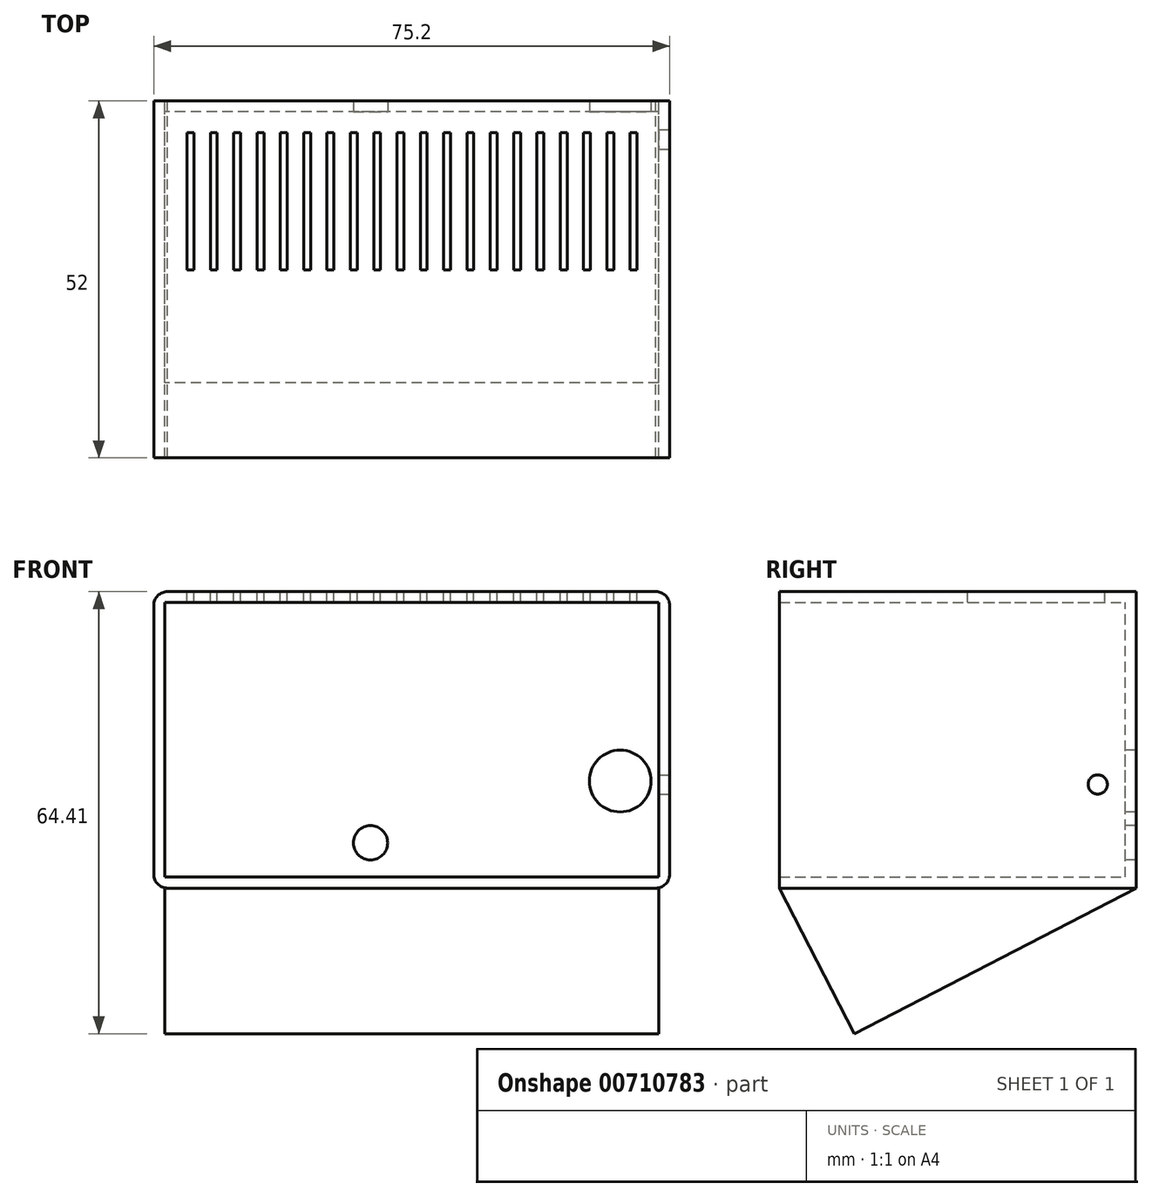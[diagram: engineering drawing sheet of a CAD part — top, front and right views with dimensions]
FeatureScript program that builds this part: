
annotation { "Feature Type Name" : "Feature", "Feature Type Description" : "" }
export const myFeature = defineFeature(function(context is Context, id is Id, definition is map)
    precondition{}
    {
        {
            var Q0;
            Q0=qCreatedBy(makeId("Front.planeOp"),FACE);
            var sketch = newSketch(context, id + "F0", { "sketchPlane" : qUnion([Q0])});
            skLineSegment(sketch, "E0.bottom", {"start": v(36, -20) * mm, "end": v(-36, -20) * mm});
            skLineSegment(sketch, "E0.top", {"start": v(36, 20) * mm, "end": v(-36, 20) * mm});
            skLineSegment(sketch, "E0.left", {"start": v(36, -20) * mm, "end": v(36, 20) * mm});
            skLineSegment(sketch, "E0.right", {"start": v(-36, -20) * mm, "end": v(-36, 20) * mm});
            skPoint(sketch, "E0.middle", {"position": v(0, 0) * mm});
            skLineSegment(sketch, "E1.0", {"start": v(-37.6, -21.6) * mm, "end": v(-37.6, 21.6) * mm});
            skLineSegment(sketch, "E1.1", {"start": v(37.6, -21.6) * mm, "end": v(-37.6, -21.6) * mm});
            skLineSegment(sketch, "E1.2", {"start": v(37.6, -21.6) * mm, "end": v(37.6, 21.6) * mm});
            skLineSegment(sketch, "E1.3", {"start": v(37.6, 21.6) * mm, "end": v(-37.6, 21.6) * mm});
            skPoint(sketch, "E2", {"position": v(30.4, -6) * mm});
            skPoint(sketch, "E3", {"position": v(-6, -15) * mm});
            skSolve(sketch);
        }
        {
            var Q0;
            Q0=makeQuery(id+"F0.imprint","IMPRINT",FACE,{"disambiguationData":[TD([[makeQuery(id+"F0.imprint","IMPRINT",EDGE,{"derivedFrom":sQuery(id+"F0.wireOp",EDGE,"E0.bottom")}),1.0]])]});
            extrude(context, id + "F1", {"entities" : qUnion([Q0]), "depth" : 52 * mm, "offsetDistance" : 25 * mm});
        }
        {
            var Q0;
            Q0=makeQuery(id+"F1.opExtrude","SWEPT_EDGE",EDGE,{"disambiguationData":[OSD([sQuery(id+"F0.wireOp",EDGE,"E1.2"),sQuery(id+"F0.wireOp",EDGE,"E1.3")])]});
            var Q1;
            Q1=makeQuery(id+"F1.opExtrude","SWEPT_EDGE",EDGE,{"disambiguationData":[OSD([sQuery(id+"F0.wireOp",EDGE,"E1.0"),sQuery(id+"F0.wireOp",EDGE,"E1.3")])]});
            var Q2;
            Q2=makeQuery(id+"F1.opExtrude","SWEPT_EDGE",EDGE,{"disambiguationData":[OSD([sQuery(id+"F0.wireOp",EDGE,"E1.0"),sQuery(id+"F0.wireOp",EDGE,"E1.1")])]});
            var Q3;
            Q3=makeQuery(id+"F1.opExtrude","SWEPT_EDGE",EDGE,{"disambiguationData":[OSD([sQuery(id+"F0.wireOp",EDGE,"E1.1"),sQuery(id+"F0.wireOp",EDGE,"E1.2")])]});
            fillet(context, id + "F2", {"entities" : qUnion([Q0, Q1, Q2, Q3]), "radius" : 2 * mm, "tangentPropagation" : true, "allowEdgeOverflow" : false});
        }
        {
            var Q0;
            Q0=makeQuery(id+"F0.imprint","IMPRINT",FACE,{"disambiguationData":[TD([[makeQuery(id+"F0.imprint","IMPRINT",EDGE,{"derivedFrom":sQuery(id+"F0.wireOp",EDGE,"E0.bottom")}),-1.0]])]});
            extrude(context, id + "F3", {"entities" : qUnion([Q0]), "operationType" : NewBodyOperationType.ADD, "depth" : 1.6 * mm, "offsetDistance" : 25 * mm});
        }
        {
            var Q0;
            Q0=qCreatedBy(makeId("Right.planeOp"),FACE);
            var sketch = newSketch(context, id + "F4", { "sketchPlane" : qUnion([Q0])});
            skPoint(sketch, "E4.0", {"position": v(-52, -21.6) * mm});
            skLineSegment(sketch, "E5", {"start": v(-52, -21.6) * mm, "end": v(-41.04, -42.8) * mm});
            skLineSegment(sketch, "E6", {"start": v(-41.04, -42.8) * mm, "end": v(0, -21.6) * mm});
            skLineSegment(sketch, "E7", {"start": v(-52, -21.6) * mm, "end": v(0, -21.6) * mm});
            skSolve(sketch);
        }
        {
            var Q0;
            Q0=makeQuery(id+"F4.imprint","IMPRINT",FACE,{"disambiguationData":[TD([[makeQuery(id+"F4.imprint","IMPRINT",EDGE,{"derivedFrom":sQuery(id+"F4.wireOp",EDGE,"E5")}),1.0]])]});
            extrude(context, id + "F5", {"entities" : qUnion([Q0]), "operationType" : NewBodyOperationType.ADD, "depth" : 72 * mm, "offsetDistance" : 25 * mm, "symmetric" : true});
        }
        {
            var Q0;
            Q0=sQuery(id+"F0.wireOp",VERTEX,"E2");
            var Q1;
            Q1=makeQuery(id+"F1.opExtrude","SWEPT_BODY",BODY,{"disambiguationData":[OSD([sQuery(id+"F0.wireOp",EDGE,"E0.bottom"),sQuery(id+"F0.wireOp",EDGE,"E0.top"),sQuery(id+"F0.wireOp",EDGE,"E0.left"),sQuery(id+"F0.wireOp",EDGE,"E0.right"),sQuery(id+"F0.wireOp",EDGE,"E1.0"),sQuery(id+"F0.wireOp",EDGE,"E1.1"),sQuery(id+"F0.wireOp",EDGE,"E1.2"),sQuery(id+"F0.wireOp",EDGE,"E1.3")])]});
            hole(context, id + "F6", {"style" : HoleStyle.SIMPLE, "endStyle" : HoleEndStyle.THROUGH, "oppositeDirection" : true, "holeDiameter" : 9 * mm, "majorDiameter" : 5 * mm, "isTappedThrough" : true, "tappedDepth" : 12 * mm, "tapClearance" : 3, "locations" : qUnion([Q0]), "scope" : qUnion([Q1])});
        }
        {
            var Q0;
            Q0=makeQuery(id+"F1.opExtrude","SWEPT_FACE",FACE,{"disambiguationData":[OSD([sQuery(id+"F0.wireOp",EDGE,"E0.left")])]});
            var sketch = newSketch(context, id + "F7", { "sketchPlane" : qUnion([Q0])});
            skPoint(sketch, "E8", {"position": v(5.6, -6.5) * mm});
            skSolve(sketch);
        }
        {
            var Q0;
            Q0=sQuery(id+"F7.wireOp",VERTEX,"E8");
            var Q1;
            Q1=makeQuery(id+"F1.opExtrude","SWEPT_BODY",BODY,{"disambiguationData":[OSD([sQuery(id+"F0.wireOp",EDGE,"E0.bottom"),sQuery(id+"F0.wireOp",EDGE,"E0.top"),sQuery(id+"F0.wireOp",EDGE,"E0.left"),sQuery(id+"F0.wireOp",EDGE,"E0.right"),sQuery(id+"F0.wireOp",EDGE,"E1.0"),sQuery(id+"F0.wireOp",EDGE,"E1.1"),sQuery(id+"F0.wireOp",EDGE,"E1.2"),sQuery(id+"F0.wireOp",EDGE,"E1.3")])]});
            hole(context, id + "F8", {"style" : HoleStyle.SIMPLE, "endStyle" : HoleEndStyle.THROUGH, "holeDiameter" : 2.8 * mm, "majorDiameter" : 5 * mm, "isTappedThrough" : true, "tappedDepth" : 12 * mm, "tapClearance" : 3, "locations" : qUnion([Q0]), "scope" : qUnion([Q1])});
        }
        {
            var Q0;
            Q0=sQuery(id+"F0.wireOp",VERTEX,"E3");
            var Q1;
            Q1=makeQuery(id+"F1.opExtrude","SWEPT_BODY",BODY,{"disambiguationData":[OSD([sQuery(id+"F0.wireOp",EDGE,"E0.bottom"),sQuery(id+"F0.wireOp",EDGE,"E0.top"),sQuery(id+"F0.wireOp",EDGE,"E0.left"),sQuery(id+"F0.wireOp",EDGE,"E0.right"),sQuery(id+"F0.wireOp",EDGE,"E1.0"),sQuery(id+"F0.wireOp",EDGE,"E1.1"),sQuery(id+"F0.wireOp",EDGE,"E1.2"),sQuery(id+"F0.wireOp",EDGE,"E1.3")])]});
            hole(context, id + "F9", {"style" : HoleStyle.SIMPLE, "endStyle" : HoleEndStyle.THROUGH, "oppositeDirection" : true, "holeDiameter" : 5 * mm, "majorDiameter" : 5 * mm, "isTappedThrough" : true, "tappedDepth" : 12 * mm, "tapClearance" : 3, "locations" : qUnion([Q0]), "scope" : qUnion([Q1])});
        }
        {
            var Q0;
            Q0=makeQuery(id+"F1.opExtrude","SWEPT_FACE",FACE,{"disambiguationData":[OSD([sQuery(id+"F0.wireOp",EDGE,"E1.3")])]});
            var sketch = newSketch(context, id + "F10", { "sketchPlane" : qUnion([Q0])});
            skLineSegment(sketch, "E9.bottom", {"start": v(-32.74, -4.6) * mm, "end": v(-31.74, -4.6) * mm});
            skLineSegment(sketch, "E9.top", {"start": v(-32.74, -24.6) * mm, "end": v(-31.74, -24.6) * mm});
            skLineSegment(sketch, "E9.left", {"start": v(-32.74, -4.6) * mm, "end": v(-32.74, -24.6) * mm});
            skLineSegment(sketch, "E9.right", {"start": v(-31.74, -4.6) * mm, "end": v(-31.74, -24.6) * mm});
            skLineSegment(sketch, "E10.1.0.0", {"start": v(-29.34, -4.6) * mm, "end": v(-28.34, -4.6) * mm});
            skLineSegment(sketch, "E10.1.0.1", {"start": v(-29.34, -4.6) * mm, "end": v(-29.34, -24.6) * mm});
            skLineSegment(sketch, "E10.1.0.2", {"start": v(-28.34, -4.6) * mm, "end": v(-28.34, -24.6) * mm});
            skLineSegment(sketch, "E10.1.0.3", {"start": v(-29.34, -24.6) * mm, "end": v(-28.34, -24.6) * mm});
            skLineSegment(sketch, "E10.2.0.0", {"start": v(-25.94, -4.6) * mm, "end": v(-24.94, -4.6) * mm});
            skLineSegment(sketch, "E10.2.0.1", {"start": v(-25.94, -4.6) * mm, "end": v(-25.94, -24.6) * mm});
            skLineSegment(sketch, "E10.2.0.2", {"start": v(-24.94, -4.6) * mm, "end": v(-24.94, -24.6) * mm});
            skLineSegment(sketch, "E10.2.0.3", {"start": v(-25.94, -24.6) * mm, "end": v(-24.94, -24.6) * mm});
            skLineSegment(sketch, "E10.3.0.0", {"start": v(-22.54, -4.6) * mm, "end": v(-21.54, -4.6) * mm});
            skLineSegment(sketch, "E10.3.0.1", {"start": v(-22.54, -4.6) * mm, "end": v(-22.54, -24.6) * mm});
            skLineSegment(sketch, "E10.3.0.2", {"start": v(-21.54, -4.6) * mm, "end": v(-21.54, -24.6) * mm});
            skLineSegment(sketch, "E10.3.0.3", {"start": v(-22.54, -24.6) * mm, "end": v(-21.54, -24.6) * mm});
            skLineSegment(sketch, "E10.4.0.0", {"start": v(-19.14, -4.6) * mm, "end": v(-18.14, -4.6) * mm});
            skLineSegment(sketch, "E10.4.0.1", {"start": v(-19.14, -4.6) * mm, "end": v(-19.14, -24.6) * mm});
            skLineSegment(sketch, "E10.4.0.2", {"start": v(-18.14, -4.6) * mm, "end": v(-18.14, -24.6) * mm});
            skLineSegment(sketch, "E10.4.0.3", {"start": v(-19.14, -24.6) * mm, "end": v(-18.14, -24.6) * mm});
            skLineSegment(sketch, "E10.5.0.0", {"start": v(-15.74, -4.6) * mm, "end": v(-14.74, -4.6) * mm});
            skLineSegment(sketch, "E10.5.0.1", {"start": v(-15.74, -4.6) * mm, "end": v(-15.74, -24.6) * mm});
            skLineSegment(sketch, "E10.5.0.2", {"start": v(-14.74, -4.6) * mm, "end": v(-14.74, -24.6) * mm});
            skLineSegment(sketch, "E10.5.0.3", {"start": v(-15.74, -24.6) * mm, "end": v(-14.74, -24.6) * mm});
            skLineSegment(sketch, "E10.6.0.0", {"start": v(-12.34, -4.6) * mm, "end": v(-11.34, -4.6) * mm});
            skLineSegment(sketch, "E10.6.0.1", {"start": v(-12.34, -4.6) * mm, "end": v(-12.34, -24.6) * mm});
            skLineSegment(sketch, "E10.6.0.2", {"start": v(-11.34, -4.6) * mm, "end": v(-11.34, -24.6) * mm});
            skLineSegment(sketch, "E10.6.0.3", {"start": v(-12.34, -24.6) * mm, "end": v(-11.34, -24.6) * mm});
            skLineSegment(sketch, "E10.7.0.0", {"start": v(-8.94, -4.6) * mm, "end": v(-7.94, -4.6) * mm});
            skLineSegment(sketch, "E10.7.0.1", {"start": v(-8.94, -4.6) * mm, "end": v(-8.94, -24.6) * mm});
            skLineSegment(sketch, "E10.7.0.2", {"start": v(-7.94, -4.6) * mm, "end": v(-7.94, -24.6) * mm});
            skLineSegment(sketch, "E10.7.0.3", {"start": v(-8.94, -24.6) * mm, "end": v(-7.94, -24.6) * mm});
            skLineSegment(sketch, "E10.8.0.0", {"start": v(-5.54, -4.6) * mm, "end": v(-4.54, -4.6) * mm});
            skLineSegment(sketch, "E10.8.0.1", {"start": v(-5.54, -4.6) * mm, "end": v(-5.54, -24.6) * mm});
            skLineSegment(sketch, "E10.8.0.2", {"start": v(-4.54, -4.6) * mm, "end": v(-4.54, -24.6) * mm});
            skLineSegment(sketch, "E10.8.0.3", {"start": v(-5.54, -24.6) * mm, "end": v(-4.54, -24.6) * mm});
            skLineSegment(sketch, "E10.9.0.0", {"start": v(-2.14, -4.6) * mm, "end": v(-1.14, -4.6) * mm});
            skLineSegment(sketch, "E10.9.0.1", {"start": v(-2.14, -4.6) * mm, "end": v(-2.14, -24.6) * mm});
            skLineSegment(sketch, "E10.9.0.2", {"start": v(-1.14, -4.6) * mm, "end": v(-1.14, -24.6) * mm});
            skLineSegment(sketch, "E10.9.0.3", {"start": v(-2.14, -24.6) * mm, "end": v(-1.14, -24.6) * mm});
            skLineSegment(sketch, "E10.10.0.0", {"start": v(1.26, -4.6) * mm, "end": v(2.26, -4.6) * mm});
            skLineSegment(sketch, "E10.10.0.1", {"start": v(1.26, -4.6) * mm, "end": v(1.26, -24.6) * mm});
            skLineSegment(sketch, "E10.10.0.2", {"start": v(2.26, -4.6) * mm, "end": v(2.26, -24.6) * mm});
            skLineSegment(sketch, "E10.10.0.3", {"start": v(1.26, -24.6) * mm, "end": v(2.26, -24.6) * mm});
            skLineSegment(sketch, "E10.11.0.0", {"start": v(4.66, -4.6) * mm, "end": v(5.66, -4.6) * mm});
            skLineSegment(sketch, "E10.11.0.1", {"start": v(4.66, -4.6) * mm, "end": v(4.66, -24.6) * mm});
            skLineSegment(sketch, "E10.11.0.2", {"start": v(5.66, -4.6) * mm, "end": v(5.66, -24.6) * mm});
            skLineSegment(sketch, "E10.11.0.3", {"start": v(4.66, -24.6) * mm, "end": v(5.66, -24.6) * mm});
            skLineSegment(sketch, "E10.12.0.0", {"start": v(8.06, -4.6) * mm, "end": v(9.06, -4.6) * mm});
            skLineSegment(sketch, "E10.12.0.1", {"start": v(8.06, -4.6) * mm, "end": v(8.06, -24.6) * mm});
            skLineSegment(sketch, "E10.12.0.2", {"start": v(9.06, -4.6) * mm, "end": v(9.06, -24.6) * mm});
            skLineSegment(sketch, "E10.12.0.3", {"start": v(8.06, -24.6) * mm, "end": v(9.06, -24.6) * mm});
            skLineSegment(sketch, "E10.13.0.0", {"start": v(11.46, -4.6) * mm, "end": v(12.46, -4.6) * mm});
            skLineSegment(sketch, "E10.13.0.1", {"start": v(11.46, -4.6) * mm, "end": v(11.46, -24.6) * mm});
            skLineSegment(sketch, "E10.13.0.2", {"start": v(12.46, -4.6) * mm, "end": v(12.46, -24.6) * mm});
            skLineSegment(sketch, "E10.13.0.3", {"start": v(11.46, -24.6) * mm, "end": v(12.46, -24.6) * mm});
            skLineSegment(sketch, "E10.14.0.0", {"start": v(14.86, -4.6) * mm, "end": v(15.86, -4.6) * mm});
            skLineSegment(sketch, "E10.14.0.1", {"start": v(14.86, -4.6) * mm, "end": v(14.86, -24.6) * mm});
            skLineSegment(sketch, "E10.14.0.2", {"start": v(15.86, -4.6) * mm, "end": v(15.86, -24.6) * mm});
            skLineSegment(sketch, "E10.14.0.3", {"start": v(14.86, -24.6) * mm, "end": v(15.86, -24.6) * mm});
            skLineSegment(sketch, "E10.15.0.0", {"start": v(18.26, -4.6) * mm, "end": v(19.26, -4.6) * mm});
            skLineSegment(sketch, "E10.15.0.1", {"start": v(18.26, -4.6) * mm, "end": v(18.26, -24.6) * mm});
            skLineSegment(sketch, "E10.15.0.2", {"start": v(19.26, -4.6) * mm, "end": v(19.26, -24.6) * mm});
            skLineSegment(sketch, "E10.15.0.3", {"start": v(18.26, -24.6) * mm, "end": v(19.26, -24.6) * mm});
            skLineSegment(sketch, "E10.16.0.0", {"start": v(21.66, -4.6) * mm, "end": v(22.66, -4.6) * mm});
            skLineSegment(sketch, "E10.16.0.1", {"start": v(21.66, -4.6) * mm, "end": v(21.66, -24.6) * mm});
            skLineSegment(sketch, "E10.16.0.2", {"start": v(22.66, -4.6) * mm, "end": v(22.66, -24.6) * mm});
            skLineSegment(sketch, "E10.16.0.3", {"start": v(21.66, -24.6) * mm, "end": v(22.66, -24.6) * mm});
            skLineSegment(sketch, "E10.17.0.0", {"start": v(25.06, -4.6) * mm, "end": v(26.06, -4.6) * mm});
            skLineSegment(sketch, "E10.17.0.1", {"start": v(25.06, -4.6) * mm, "end": v(25.06, -24.6) * mm});
            skLineSegment(sketch, "E10.17.0.2", {"start": v(26.06, -4.6) * mm, "end": v(26.06, -24.6) * mm});
            skLineSegment(sketch, "E10.17.0.3", {"start": v(25.06, -24.6) * mm, "end": v(26.06, -24.6) * mm});
            skLineSegment(sketch, "E10.18.0.0", {"start": v(28.46, -4.6) * mm, "end": v(29.46, -4.6) * mm});
            skLineSegment(sketch, "E10.18.0.1", {"start": v(28.46, -4.6) * mm, "end": v(28.46, -24.6) * mm});
            skLineSegment(sketch, "E10.18.0.2", {"start": v(29.46, -4.6) * mm, "end": v(29.46, -24.6) * mm});
            skLineSegment(sketch, "E10.18.0.3", {"start": v(28.46, -24.6) * mm, "end": v(29.46, -24.6) * mm});
            skLineSegment(sketch, "E10.19.0.0", {"start": v(31.86, -4.6) * mm, "end": v(32.86, -4.6) * mm});
            skLineSegment(sketch, "E10.19.0.1", {"start": v(31.86, -4.6) * mm, "end": v(31.86, -24.6) * mm});
            skLineSegment(sketch, "E10.19.0.2", {"start": v(32.86, -4.6) * mm, "end": v(32.86, -24.6) * mm});
            skLineSegment(sketch, "E10.19.0.3", {"start": v(31.86, -24.6) * mm, "end": v(32.86, -24.6) * mm});
            skLineSegment(sketch, "E10.direction1", {"start": v(-32.74, -4.6) * mm, "end": v(-29.34, -4.6) * mm, "construction": true});
            skSolve(sketch);
        }
        {
            var Q0;
            Q0=makeQuery(id+"F10.imprint","IMPRINT",FACE,{"disambiguationData":[TD([[makeQuery(id+"F10.imprint","IMPRINT",EDGE,{"derivedFrom":sQuery(id+"F10.wireOp",EDGE,"E9.bottom")}),-1.0]])]});
            var Q1;
            Q1=makeQuery(id+"F10.imprint","IMPRINT",FACE,{"disambiguationData":[TD([[makeQuery(id+"F10.imprint","IMPRINT",EDGE,{"derivedFrom":sQuery(id+"F10.wireOp",EDGE,"E10.1.0.0")}),-1.0]])]});
            var Q2;
            Q2=makeQuery(id+"F10.imprint","IMPRINT",FACE,{"disambiguationData":[TD([[makeQuery(id+"F10.imprint","IMPRINT",EDGE,{"derivedFrom":sQuery(id+"F10.wireOp",EDGE,"E10.2.0.0")}),-1.0]])]});
            var Q3;
            Q3=makeQuery(id+"F10.imprint","IMPRINT",FACE,{"disambiguationData":[TD([[makeQuery(id+"F10.imprint","IMPRINT",EDGE,{"derivedFrom":sQuery(id+"F10.wireOp",EDGE,"E10.3.0.0")}),-1.0]])]});
            var Q4;
            Q4=makeQuery(id+"F10.imprint","IMPRINT",FACE,{"disambiguationData":[TD([[makeQuery(id+"F10.imprint","IMPRINT",EDGE,{"derivedFrom":sQuery(id+"F10.wireOp",EDGE,"E10.4.0.0")}),-1.0]])]});
            var Q5;
            Q5=makeQuery(id+"F10.imprint","IMPRINT",FACE,{"disambiguationData":[TD([[makeQuery(id+"F10.imprint","IMPRINT",EDGE,{"derivedFrom":sQuery(id+"F10.wireOp",EDGE,"E10.5.0.0")}),-1.0]])]});
            var Q6;
            Q6=makeQuery(id+"F10.imprint","IMPRINT",FACE,{"disambiguationData":[TD([[makeQuery(id+"F10.imprint","IMPRINT",EDGE,{"derivedFrom":sQuery(id+"F10.wireOp",EDGE,"E10.6.0.0")}),-1.0]])]});
            var Q7;
            Q7=makeQuery(id+"F10.imprint","IMPRINT",FACE,{"disambiguationData":[TD([[makeQuery(id+"F10.imprint","IMPRINT",EDGE,{"derivedFrom":sQuery(id+"F10.wireOp",EDGE,"E10.7.0.0")}),-1.0]])]});
            var Q8;
            Q8=makeQuery(id+"F10.imprint","IMPRINT",FACE,{"disambiguationData":[TD([[makeQuery(id+"F10.imprint","IMPRINT",EDGE,{"derivedFrom":sQuery(id+"F10.wireOp",EDGE,"E10.8.0.0")}),-1.0]])]});
            var Q9;
            Q9=makeQuery(id+"F10.imprint","IMPRINT",FACE,{"disambiguationData":[TD([[makeQuery(id+"F10.imprint","IMPRINT",EDGE,{"derivedFrom":sQuery(id+"F10.wireOp",EDGE,"E10.10.0.0")}),-1.0]])]});
            var Q10;
            Q10=makeQuery(id+"F10.imprint","IMPRINT",FACE,{"disambiguationData":[TD([[makeQuery(id+"F10.imprint","IMPRINT",EDGE,{"derivedFrom":sQuery(id+"F10.wireOp",EDGE,"E10.11.0.0")}),-1.0]])]});
            var Q11;
            Q11=makeQuery(id+"F10.imprint","IMPRINT",FACE,{"disambiguationData":[TD([[makeQuery(id+"F10.imprint","IMPRINT",EDGE,{"derivedFrom":sQuery(id+"F10.wireOp",EDGE,"E10.9.0.0")}),-1.0]])]});
            var Q12;
            Q12=makeQuery(id+"F10.imprint","IMPRINT",FACE,{"disambiguationData":[TD([[makeQuery(id+"F10.imprint","IMPRINT",EDGE,{"derivedFrom":sQuery(id+"F10.wireOp",EDGE,"E10.12.0.0")}),-1.0]])]});
            var Q13;
            Q13=makeQuery(id+"F10.imprint","IMPRINT",FACE,{"disambiguationData":[TD([[makeQuery(id+"F10.imprint","IMPRINT",EDGE,{"derivedFrom":sQuery(id+"F10.wireOp",EDGE,"E10.13.0.0")}),-1.0]])]});
            var Q14;
            Q14=makeQuery(id+"F10.imprint","IMPRINT",FACE,{"disambiguationData":[TD([[makeQuery(id+"F10.imprint","IMPRINT",EDGE,{"derivedFrom":sQuery(id+"F10.wireOp",EDGE,"E10.14.0.0")}),-1.0]])]});
            var Q15;
            Q15=makeQuery(id+"F10.imprint","IMPRINT",FACE,{"disambiguationData":[TD([[makeQuery(id+"F10.imprint","IMPRINT",EDGE,{"derivedFrom":sQuery(id+"F10.wireOp",EDGE,"E10.15.0.0")}),-1.0]])]});
            var Q16;
            Q16=makeQuery(id+"F10.imprint","IMPRINT",FACE,{"disambiguationData":[TD([[makeQuery(id+"F10.imprint","IMPRINT",EDGE,{"derivedFrom":sQuery(id+"F10.wireOp",EDGE,"E10.16.0.0")}),-1.0]])]});
            var Q17;
            Q17=makeQuery(id+"F10.imprint","IMPRINT",FACE,{"disambiguationData":[TD([[makeQuery(id+"F10.imprint","IMPRINT",EDGE,{"derivedFrom":sQuery(id+"F10.wireOp",EDGE,"E10.17.0.0")}),-1.0]])]});
            var Q18;
            Q18=makeQuery(id+"F10.imprint","IMPRINT",FACE,{"disambiguationData":[TD([[makeQuery(id+"F10.imprint","IMPRINT",EDGE,{"derivedFrom":sQuery(id+"F10.wireOp",EDGE,"E10.18.0.0")}),-1.0]])]});
            var Q19;
            Q19=makeQuery(id+"F10.imprint","IMPRINT",FACE,{"disambiguationData":[TD([[makeQuery(id+"F10.imprint","IMPRINT",EDGE,{"derivedFrom":sQuery(id+"F10.wireOp",EDGE,"E10.19.0.0")}),-1.0]])]});
            extrude(context, id + "F11", {"entities" : qUnion([Q0, Q1, Q2, Q3, Q4, Q5, Q6, Q7, Q8, Q9, Q10, Q11, Q12, Q13, Q14, Q15, Q16, Q17, Q18, Q19]), "operationType" : NewBodyOperationType.REMOVE, "oppositeDirection" : true, "depth" : 25 * mm, "offsetDistance" : 25 * mm});
        }
    });
